# Revit family: Rough_In_Valve-Integrated-GROHE-Grohsafe-35117
name_source: partatom
category: Pipe Accessories
units: mm (PartAtom-declared; Revit-internal decimal feet)

## family parameters
Always vertical = No
Cut with Voids When Loaded = No
OmniClass Number = 23.65.70.00
OmniClass Title = Terminals for Supplied Liquids and Gases
Part Type = Normal
Round Connector Dimension = Use Diameter
Shared = Yes
Work Plane-Based = Yes

## types (1)
- 35117000
    2-Way = Yes
    3-Way = No
    3-Way Tempered Connection = 0"
    Assembly Code = D2020
    CW Connection = Yes
    CWFU = 2
    Cold Water Connection Diameter = 1/2"
    Default Elevation = 0"
    Description = Grohsafe Pressure Balance Rough-In Valve with Integrated Diverter
    Diverter Constraint = 1/4"
    Finish = Metal-Grohe-Grey
    HW Connection = Yes
    HWFU = 3
    Height = 9 1/2"
    Hot Water Connection Diameter = 1"
    IAPMO Compliance = Massachusetts Plumbing Board Approved, ASSE 1016, CSA B125.1, CSA B125.16, ASME A112.18.1, ASME A112.1016
    Manufacturer = GROHE
    Material = Metal-Grohe-Grey
    Model = 35117000
    Price = Prices may vary. Please consult Manufacturer Representative for most up-to-date price list.
    Tempered Water Connection = Yes
    Tempered Water Connection Diameter = 1/2"
    URL = https://www.grohe.us
    Vent Connection = No
    WFU = 4
    Waste Connection = No
    Width = 4 27/32"

## geometry (parser evidence)
native form markers: Sweep x2
no freeform markers — native parametric forms only
